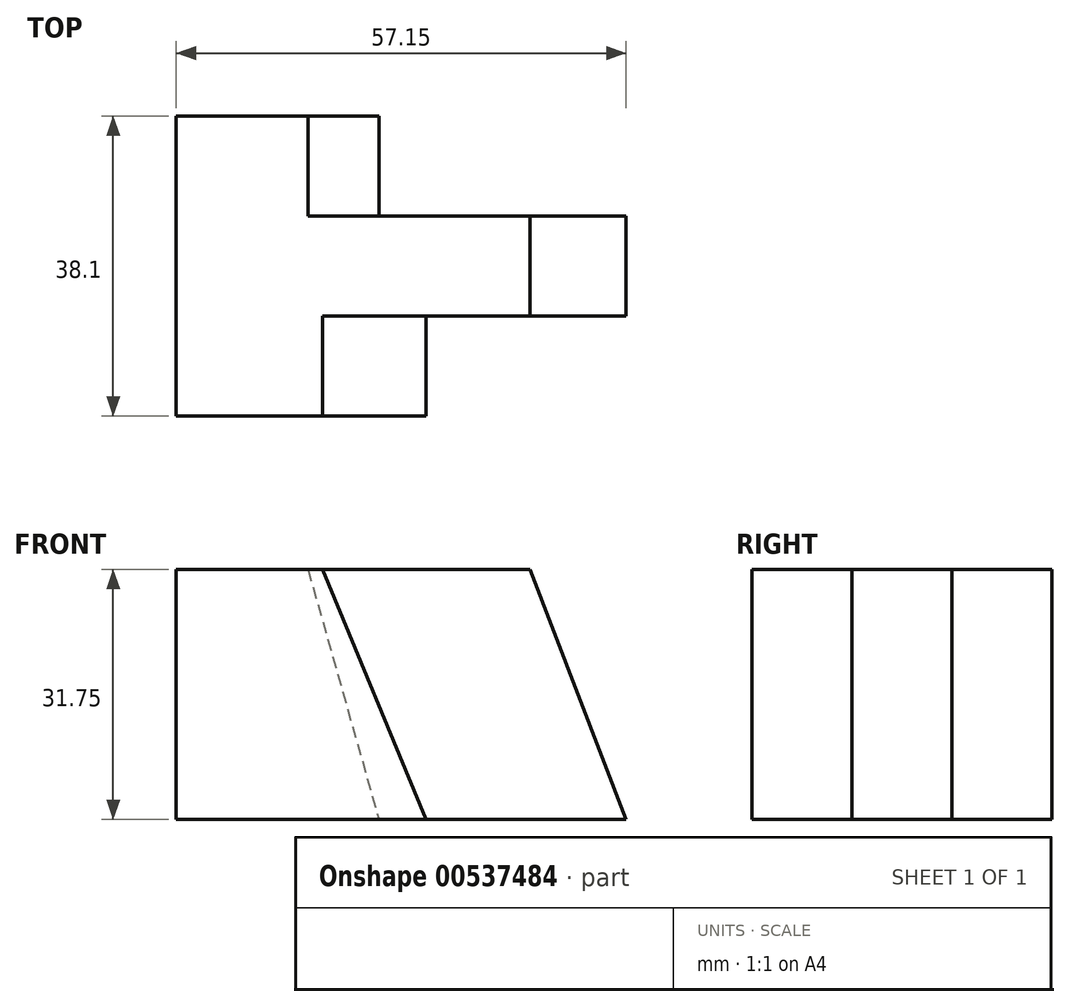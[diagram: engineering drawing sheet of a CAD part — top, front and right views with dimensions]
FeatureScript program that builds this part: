
annotation { "Feature Type Name" : "Feature", "Feature Type Description" : "" }
export const myFeature = defineFeature(function(context is Context, id is Id, definition is map)
    precondition{}
    {
        {
            var Q0;
            Q0=qCreatedBy(makeId("Front.planeOp"),FACE);
            var sketch = newSketch(context, id + "F0", { "sketchPlane" : qUnion([Q0])});
            skLineSegment(sketch, "E0", {"start": v(0, 0) * mm, "end": v(57.15, 0) * mm});
            skLineSegment(sketch, "E1", {"start": v(57.15, 0) * mm, "end": v(57.15, 31.75) * mm});
            skLineSegment(sketch, "E2", {"start": v(57.15, 31.75) * mm, "end": v(0, 31.75) * mm});
            skLineSegment(sketch, "E3", {"start": v(0, 31.75) * mm, "end": v(0, 0) * mm});
            skSolve(sketch);
        }
        {
            var Q0;
            Q0=makeQuery(id+"F0.imprint","IMPRINT",FACE,{"disambiguationData":[TD([[makeQuery(id+"F0.imprint","IMPRINT",EDGE,{"derivedFrom":sQuery(id+"F0.wireOp",EDGE,"E0")}),1.0]])]});
            extrude(context, id + "F1", {"entities" : qUnion([Q0]), "depth" : 38.1 * mm, "offsetDistance" : 25.4 * mm});
        }
        {
            var Q0;
            Q0=makeQuery(id+"F1.opExtrude","CAP_FACE",FACE,{"disambiguationData":[OSD([sQuery(id+"F0.wireOp",EDGE,"E0"),sQuery(id+"F0.wireOp",EDGE,"E1"),sQuery(id+"F0.wireOp",EDGE,"E2"),sQuery(id+"F0.wireOp",EDGE,"E3")])],"isStart":false});
            var sketch = newSketch(context, id + "F2", { "sketchPlane" : qUnion([Q0])});
            skLineSegment(sketch, "E4", {"start": v(57.15, 0) * mm, "end": v(44.97, 31.75) * mm});
            skLineSegment(sketch, "E5", {"start": v(44.97, 31.75) * mm, "end": v(18.6, 31.75) * mm});
            skLineSegment(sketch, "E6", {"start": v(57.15, 0) * mm, "end": v(31.75, 0) * mm});
            skLineSegment(sketch, "E7", {"start": v(18.6, 31.75) * mm, "end": v(31.75, 0) * mm});
            skSolve(sketch);
        }
        {
            var Q0;
            Q0=makeQuery(id+"F2.imprint","IMPRINT",FACE,{"disambiguationData":[TD([[makeQuery(id+"F2.imprint","IMPRINT",EDGE,{"derivedFrom":sQuery(id+"F2.wireOp",EDGE,"E4")}),1.0]])]});
            extrude(context, id + "F3", {"entities" : qUnion([Q0]), "operationType" : NewBodyOperationType.REMOVE, "oppositeDirection" : true, "depth" : 12.7 * mm, "offsetDistance" : 25.4 * mm});
        }
        {
            var Q0;
            {var subQ0=sQuery(id+"F0.wireOp",EDGE,"E1");var subQ1=sQuery(id+"F0.wireOp",EDGE,"E2");Q0=makeQuery(id+"F3.boolean.opBoolean","SPLIT",FACE,{"disambiguationData":[TD([makeQuery(id+"F1.opExtrude","SWEPT_FACE",FACE,{"disambiguationData":[OSD([subQ0])]})])],"derivedFrom":makeQuery(id+"F1.opExtrude","CAP_FACE",FACE,{"disambiguationData":[OSD([sQuery(id+"F0.wireOp",EDGE,"E0"),subQ0,subQ1,sQuery(id+"F0.wireOp",EDGE,"E3")])],"isStart":false})});}
            var sketch = newSketch(context, id + "F4", { "sketchPlane" : qUnion([Q0])});
            skLineSegment(sketch, "E8", {"start": v(57.15, 31.75) * mm, "end": v(44.97, 31.75) * mm});
            skLineSegment(sketch, "E9", {"start": v(44.97, 31.75) * mm, "end": v(57.15, 0) * mm});
            skLineSegment(sketch, "E10", {"start": v(57.15, 0) * mm, "end": v(57.15, 31.75) * mm});
            skSolve(sketch);
        }
        {
            var Q0;
            Q0=makeQuery(id+"F4.imprint","IMPRINT",FACE,{"disambiguationData":[TD([[makeQuery(id+"F4.imprint","IMPRINT",EDGE,{"derivedFrom":sQuery(id+"F4.wireOp",EDGE,"E8")}),1.0]])]});
            extrude(context, id + "F5", {"entities" : qUnion([Q0]), "operationType" : NewBodyOperationType.REMOVE, "oppositeDirection" : true, "depth" : 38.1 * mm, "offsetDistance" : 25.4 * mm});
        }
        {
            var Q0;
            Q0=makeQuery(id+"F1.opExtrude","CAP_FACE",FACE,{"disambiguationData":[OSD([sQuery(id+"F0.wireOp",EDGE,"E0"),sQuery(id+"F0.wireOp",EDGE,"E1"),sQuery(id+"F0.wireOp",EDGE,"E2"),sQuery(id+"F0.wireOp",EDGE,"E3")])],"isStart":true});
            var sketch = newSketch(context, id + "F6", { "sketchPlane" : qUnion([Q0])});
            skLineSegment(sketch, "E11", {"start": v(-16.75, 31.75) * mm, "end": v(-25.74, 0) * mm});
            skLineSegment(sketch, "E12", {"start": v(-25.74, 0) * mm, "end": v(-57.15, 0) * mm});
            skLineSegment(sketch, "E13", {"start": v(-57.15, 0) * mm, "end": v(-44.97, 31.75) * mm});
            skLineSegment(sketch, "E14", {"start": v(-44.97, 31.75) * mm, "end": v(-16.75, 31.75) * mm});
            skSolve(sketch);
        }
        {
            var Q0;
            Q0=makeQuery(id+"F6.imprint","IMPRINT",FACE,{"disambiguationData":[TD([[makeQuery(id+"F6.imprint","IMPRINT",EDGE,{"derivedFrom":sQuery(id+"F6.wireOp",EDGE,"E11")}),-1.0]])]});
            extrude(context, id + "F7", {"entities" : qUnion([Q0]), "operationType" : NewBodyOperationType.REMOVE, "oppositeDirection" : true, "depth" : 12.7 * mm, "offsetDistance" : 25.4 * mm});
        }
    });
